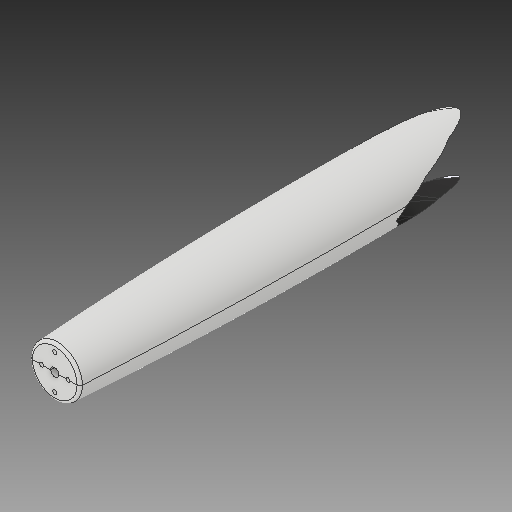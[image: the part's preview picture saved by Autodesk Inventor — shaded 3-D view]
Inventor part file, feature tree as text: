
AUTODESK INVENTOR PART (.ipt)
format: ipt  version: 2017 (Build 210142000, 142)  size: 2,186,752 bytes
history: native  units: in
note: dims shown in document units (in); Inventor stores cm internally (conversion verified against a paired STEP export)
features: reference x7, plane x6, other x6, sketch x5, extrude x4, projected_geometry x4, loft x1, fillet x1, surface_op x1, split x1, move_body x1
ambient origin geometry x8: Origin, YZ Plane, XZ Plane, XY Plane, X Axis, Y Axis, Z Axis, Center Point
bodies: Solid2 (feature_tree), Solid5 (feature_tree), Solid6 (feature_tree)
feature tree (37):
  plane  "Work Plane5"
  extrude  "Extrusion3"  Depth=1.4173in
  plane  "Work Plane7"
  loft  "Loft2"
  plane  "Work Plane8"
  extrude  "Extrusion4"  Depth=0.1181in
  extrude  "Extrusion8"  TaperAngle=90.0deg  [1 undecoded]
  plane  "Work Plane9"
  fillet  "Fillet1"  Radius=0.748in
  extrude  "Extrusion9"  Depth=0.3937in
  surface_op  "Sculpt2"
  plane  "Work Plane10"
  split  "Split2"
  move_body  "Move Body2"
  sketch  "Sketch5"  dims[d21=2.7559in d22=1.4173in]
  reference  "Reference17"
  reference  "Reference18"
  reference  "Reference19"
  reference  "Reference20"
  reference  "Reference21"
  reference  "Reference22"
  reference  "Reference23"
  plane  "Work Plane6"
  sketch  "Sketch6"  dims[d23=0.9843in d24=0.1181in]
  sketch  "Sketch7"  dims[d25=0.1181in d26=0.1181in]
  other  "Edges2"
  sketch  "Sketch14"  dims[d27=0.1181in d28=90.0deg d29=0.748in]
  projected_geometry  "Projected Loop4"
  projected_geometry  "Projected Loop5"
  projected_geometry  "Projected Loop6"
  sketch  "Sketch17"  dims[d30=5.3691in d31=0.0in d32=2.5in d33=3.8125in d34=0.0in d35=90.0deg d36=0.0in d37=90.0deg d38=0.0in d39=90.0deg d40=0.9843in d41=0.748in d42=0.1181in d43=0.1181in d44=0.1181in d45=0.1181in d46=0.4975in d47=0.0in d63=6.5438in d64=0.0in d67=0.0in d71=9.8425in d72=0.0787in d73=0.2362in d74=0.9188in d75=0.0in d76=0.25in d77=0.0in d78=0.3937in d79=0.0in]
  projected_geometry  "Projected Loop7"
  other  "<userpath>\ownCloud\pfc\projeto\asa1\assembly2.iam"
  other  "assembly2.iam"
  other  "Part1:1"
  other  "Composite2"
  other  "Srf2"
note: 1 required parameter value undecoded (feature->parameter linkage not recoverable at this tier; creation-order binding heuristic only, values carry confidence <= 0.55)
